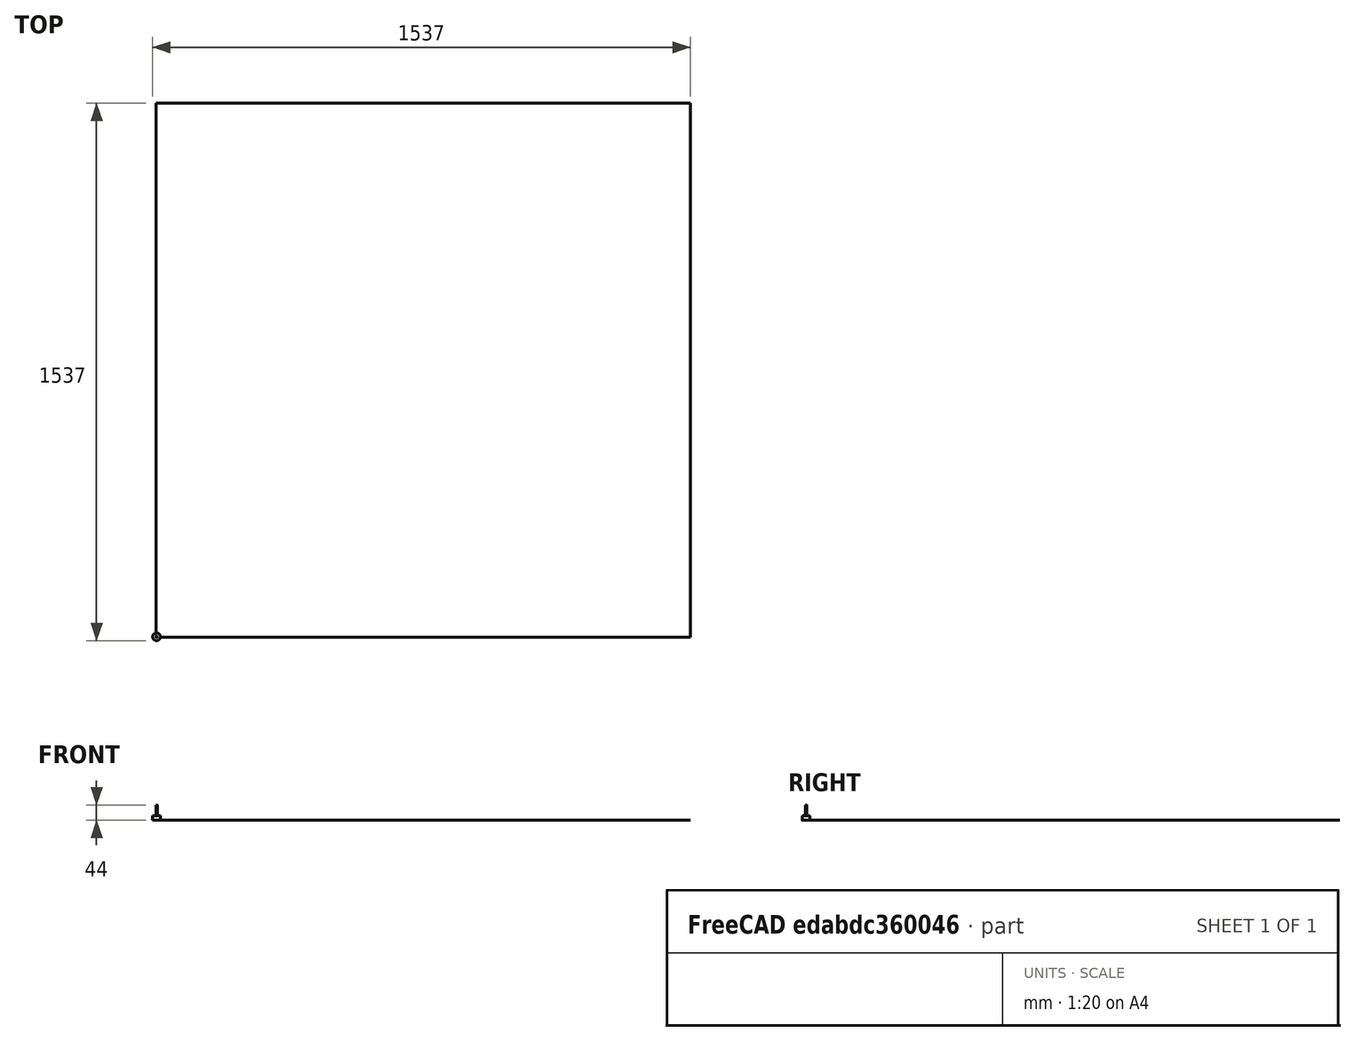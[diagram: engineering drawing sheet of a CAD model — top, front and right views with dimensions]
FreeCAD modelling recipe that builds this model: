
FCSTD DOCUMENT  (FreeCAD 0.22R37100 (Git))
Label: table_prepare2
License: All rights reserved
LicenseURL: http://en.wikipedia.org/wiki/All_rights_reserved
objects: Part::FeaturePython×3, App::DocumentObjectGroup×3, Path::FeaturePython×3, Part::Plane×1, App::FeaturePython×1
note: 5 computed .brp shape members not serialized (recipe doc carries the construction recipe); baked Part::Feature solids carry a one-line shape summary decoded from their .brp

FEATURE [Part::Plane] Plane
  AttacherType = Attacher::AttachEngine3D
  Length = 1525
  Width = 1525
FEATURE [App::FeaturePython] SetupSheet  # Path/CAM operation (typed FeaturePython)
  ClearanceHeightExpression = OpStockZMax+SetupSheet.ClearanceHeightOffset
  ClearanceHeightOffset = 5
  CoolantMode = 0
  CoolantModes = None | Flood | Mist
  FinalDepthExpression = OpFinalDepth
  HorizRapid = 0
  ProfileDirection = 1
  ProfileprocessCircles = true
  ProfileprocessHoles = true
  ProfileprocessPerimeter = true
  SafeHeightExpression = OpStockZMax+SetupSheet.SafeHeightOffset
  SafeHeightOffset = 3
  StartDepthExpression = OpStartDepth
  StepDownExpression = OpToolDiameter
  VertRapid = 0
FEATURE [Part::FeaturePython] Clone  label="Model-Plane"  # Draft clone (typed FeaturePython)
  AttacherType = Attacher::AttachEngine3D
  Fuse = false
  Objects = -> [Plane]
  PathResource = Model
  Placement = pos=(-1525,0,0) rot=(0,0,1;0rad)
  Scale = (1,1,1)
FEATURE [App::DocumentObjectGroup] Model
  Group = -> [Clone]
FEATURE [Part::FeaturePython] Stock  # WARN: FeaturePython — macro-defined, semantics opaque (R4)
  Base = -> Model
  ExtXneg = 1
  ExtXpos = 1
  ExtYneg = 1
  ExtYpos = 1
  ExtZneg = 0
  ExtZpos = 1
  StockType = FromBase
FEATURE [Part::FeaturePython] ToolBit001  label="22mm Endmill005"  # Path/CAM toolbit (typed FeaturePython)
  BitPropertyNames = Chipload | CuttingEdgeHeight | Diameter | Flutes | Length | Material | ShankDiameter | SpindleDirection
  BitShape = <path>
  Chipload = 0
  CuttingEdgeHeight = 13
  Diameter = 40
  File = <userpath>/.local/share/FreeCAD/Macro/Bit/22mm_Endmill.fctb
  Flutes = 0
  Length = 44
  Material = 0
  ShankDiameter = 4
  ShapeName = endmill
  SpindleDirection = 0
FEATURE [Path::FeaturePython] _2mm_Endmill005  label="22mm Endmill006"  # Path/CAM operation (typed FeaturePython)
  HorizFeed = 100
  HorizRapid = 0
  SpindleDir = 0
  SpindleSpeed = 15000
  Tool = -> ToolBit001
  ToolNumber = 2
  VertFeed = 50
  VertRapid = 0
  expr: HorizRapid = SetupSheet.HorizRapid
  expr: VertRapid = SetupSheet.VertRapid
FEATURE [App::DocumentObjectGroup] Tools
  Group = -> [_2mm_Endmill005]
FEATURE [Path::FeaturePython] MillFace  # Path/CAM operation (typed FeaturePython)
  Active = true
  AreaParams:
    Tolerance = 1e-07
    FitArcs = True
    Simplify = False
    CleanDistance = 0.0
    Accuracy = 0.01
    Unit = 1.0
    MinArcPoints = 4
    MaxArcPoints = 100
    ClipperScale = 10000000.0
    Fill = 0
    Coplanar = 0
    Reorient = True
    Outline = False
    Explode = False
    OpenMode = 0
    Deflection = 0.01
    SubjectFill = 0
    ClipFill = 0
    Offset = 0.0
    ExtraPass = 0
    Stepover = 0.0
    LastStepover = 0.0
    JoinType = 0
    EndType = 0
    MiterLimit = 2.0
    RoundPrecision = 0.0
    PocketMode = 1
    ToolRadius = 20.0
    PocketExtraOffset = 0.0
    PocketStepover = 32.0
    PocketLastStepover = 0.0
    FromCenter = True
    Angle = 0.0
    AngleShift = 0.0
    Shift = 0.0
    Thicken = False
    SectionCount = -1
    Stepdown = 1.0
    SectionOffset = 0.0
    SectionTolerance = 1e-06
    SectionMode = 2
    Project = False
  Base = -> [Clone]
  BoundaryShape = 1
  ClearEdges = true
  ClearanceHeight = 6
  CoolantMode = 0
  CutMode = 0
  CycleTime = 00:12:58
  ExcludeRaisedAreas = false
  ExtraOffset = 0
  FinalDepth = -0.1
  FinishDepth = 0
  KeepToolDown = false
  MinTravel = true
  OffsetPattern = 0
  OpFinalDepth = 0
  OpStartDepth = 1
  OpStockZMax = 1
  OpStockZMin = 0
  OpToolDiameter = 40
  PathParams = {'orientation': 1, 'sort_mode': 3, 'threshold': 40.0, 'feedrate': 100.0, 'feedrate_v': 50.0, 'verbose': True, 'resume_height': 4.0, 'retraction': 6.0, 'return_end': True, 'preamble': False, 'start': Vector (0.0, 0.0, 0.0)}
  PocketLastStepOver = 0
  SafeHeight = 4
  SplitArcs = false
  StartAt = 0
  StartDepth = 1
  StartPoint = (0,0,0)
  StepDown = 40
  StepOver = 80
  ToolController = -> _2mm_Endmill005
  UseRestMachining = false
  UseStartPoint = true
  ZigZagAngle = 0
  expr: ClearanceHeight = OpStockZMax + SetupSheet.ClearanceHeightOffset
  expr: FinalDepth = -0.1 mm
  expr: SafeHeight = OpStockZMax + SetupSheet.SafeHeightOffset
  expr: StartDepth = OpStartDepth
  expr: StepDown = OpToolDiameter
FEATURE [App::DocumentObjectGroup] Operations
  Group = -> [MillFace]
FEATURE [Path::FeaturePython] Job  # Path/CAM operation (typed FeaturePython)
  CycleTime = 00:12:58
  Fixtures = G54
  GeometryTolerance = 0.01
  JobType = 0
  LastPostProcessDate = 2024-09-17 12:50:43.171286
  LastPostProcessOutput = <path>
  Model = -> Model
  Operations = -> Operations
  OrderOutputBy = 0
  PostProcessor = 1
  PostProcessorArgs = --axis-modal --modal
  PostProcessorOutputFile = <path>
  SetupSheet = -> SetupSheet
  SplitOutput = false
  Stock = -> Stock
  Tools = -> Tools
note: 3 file-system paths scrubbed to <path> (originals preserved in the JSON sidecar)
